# Revit family: FU_Table_Sandler_Cono 4004 - Complete
name_source: partatom
category: Furniture
units: mm (PartAtom-declared; Revit-internal decimal feet)

## family parameters
Always vertical = Yes
Cut with Voids When Loaded = No
OmniClass Number = 23.40.20.00
OmniClass Title = General Furniture and Specialties
Render Appearance Source = Family Geometry
Room Calculation Point = No
Shared = No
Work Plane-Based = No

## types (3) — shared parameters
Depth = 310 mm  [stored 1.01706 ft]
Height = 550 mm
Manufacturer = Sandler
URL = https://www.sandlerseating.com
Width = 310 mm  [stored 1.01706 ft]
zero-valued in all types: Default Elevation

## per-type parameters (varying)
| type | Description | Model | Top Type |
| Cono 4004 - D24 | Coffee table with metal base and 60cm/24"-diameter table top. 45cm/17.75" high. The round table top is available in woodgrain or a lacquered finish, with a reverse knife edge profile. Other profiles and materials available by special request. | Cono 4004 D24 | FU_Top_Sandler_EF125 : 125EF Top 60dia |
| Cono 4004 - D28 | Coffee table with metal base and 70cm/28"-diameter table top. 45cm/17.75" high. The round table top is available in woodgrain or a lacquered finish, with a reverse knife edge profile. Other profiles and materials available by special request. | Cono 4004 D28 | FU_Top_Sandler_EF125 : 125EF Top 70dia |
| Cono 4004 - D32 | Coffee table with metal base and 80cm/32"-diameter table top. 45cm/17.75" high. The round table top is available in woodgrain or a lacquered finish, with a reverse knife edge profile. Other profiles and materials available by special request. | Cono 4004 D32 | FU_Top_Sandler_EF125 : 125EF Top 80dia |

note: [stored X ft] marks values corroborated as IEEE doubles in the binary element streams (Revit-internal decimal feet)

## geometry (parser evidence)
native form markers: Sweep x8
no freeform markers — native parametric forms only
